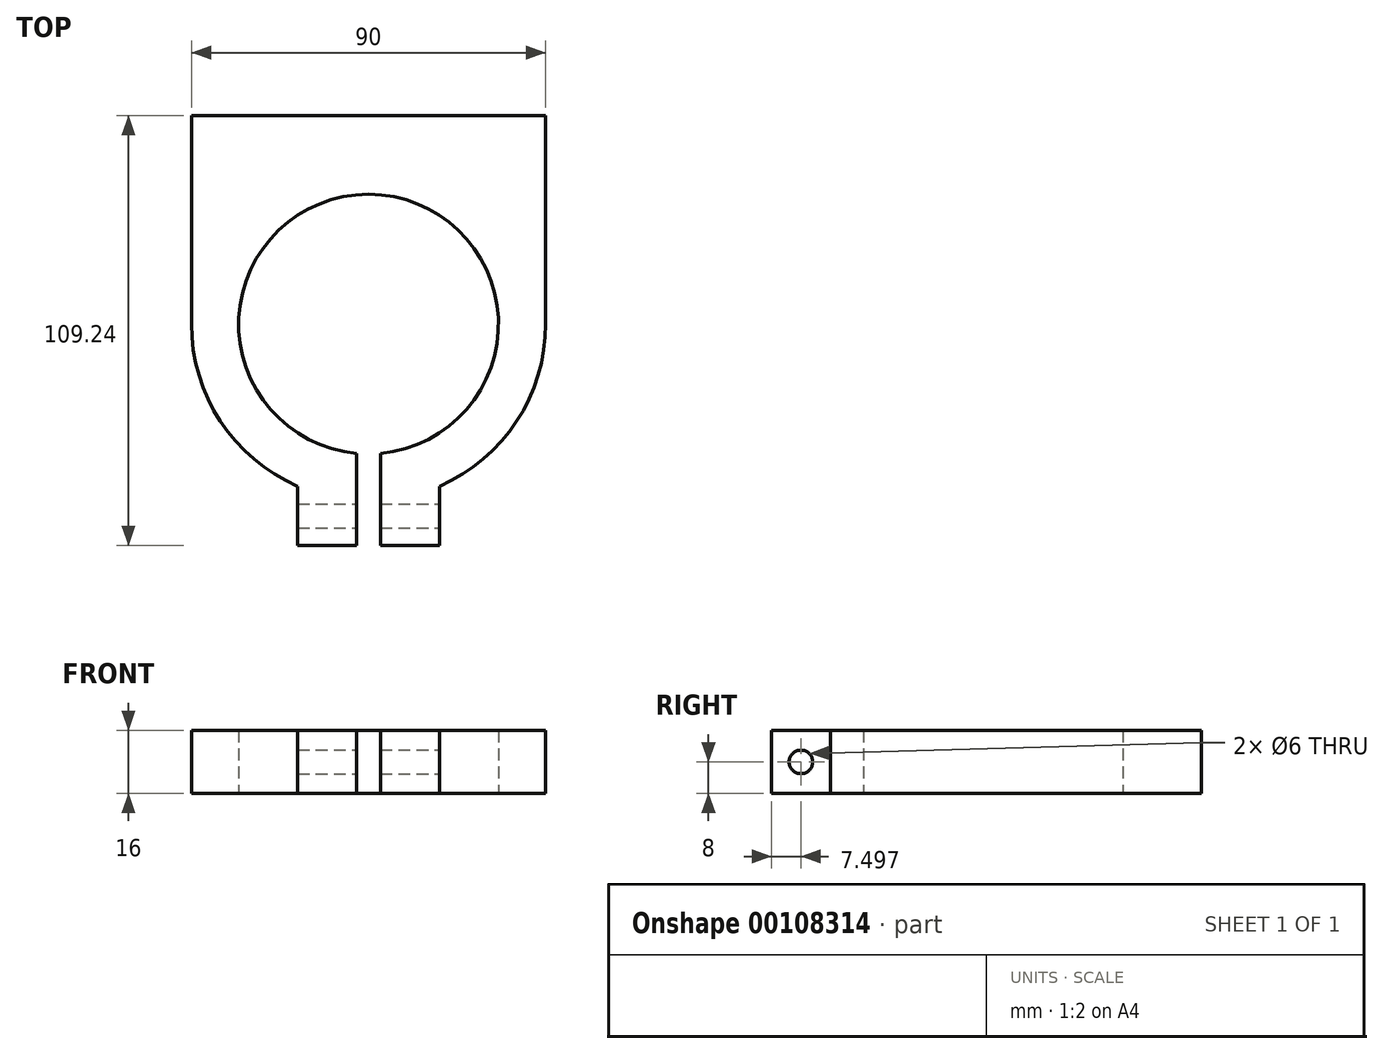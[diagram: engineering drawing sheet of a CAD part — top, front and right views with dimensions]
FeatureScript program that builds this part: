
annotation { "Feature Type Name" : "Feature", "Feature Type Description" : "" }
export const myFeature = defineFeature(function(context is Context, id is Id, definition is map)
    precondition{}
    {
        {
            var Q0;
            Q0=qCreatedBy(makeId("Top.planeOp"),FACE);
            var sketch = newSketch(context, id + "F0", { "sketchPlane" : qUnion([Q0])});
            skLineSegment(sketch, "E0", {"start": v(-45, 0) * mm, "end": v(-45, 53) * mm});
            skLineSegment(sketch, "E1", {"start": v(-45, 53) * mm, "end": v(0, 53) * mm});
            skLineSegment(sketch, "E2", {"start": v(-3, -32.86) * mm, "end": v(-3, -56.24) * mm});
            skLineSegment(sketch, "E3", {"start": v(-3, -56.24) * mm, "end": v(-18, -56.24) * mm});
            skLineSegment(sketch, "E4", {"start": v(-18, -56.24) * mm, "end": v(-18, -41.24) * mm});
            skArc(sketch, "E5", {"start": v(-3, -32.86) * mm, "mid": v(-32.97, 1.5) * mm, "end": v(0, 33) * mm});
            skArc(sketch, "E6", {"start": v(-45, 0) * mm, "mid": v(-37.65, -24.65) * mm, "end": v(-18, -41.24) * mm});
            skLineSegment(sketch, "E7.MirrorCS", {"start": v(18, -56.24) * mm, "end": v(18, -41.24) * mm});
            skArc(sketch, "E8.MirrorCS", {"start": v(3, -32.86) * mm, "mid": v(32.97, 1.5) * mm, "end": v(0, 33) * mm});
            skLineSegment(sketch, "E9.MirrorCS", {"start": v(45, 0) * mm, "end": v(45, 53) * mm});
            skArc(sketch, "E10.MirrorCS", {"start": v(45, 0) * mm, "mid": v(37.65, -24.65) * mm, "end": v(18, -41.24) * mm});
            skLineSegment(sketch, "E11.MirrorCS", {"start": v(45, 53) * mm, "end": v(0, 53) * mm});
            skLineSegment(sketch, "E12.MirrorCS", {"start": v(3, -32.86) * mm, "end": v(3, -56.24) * mm});
            skLineSegment(sketch, "E13.MirrorCS", {"start": v(3, -56.24) * mm, "end": v(18, -56.24) * mm});
            skSolve(sketch);
        }
        {
            var Q0;
            Q0=makeQuery(id+"F0.imprint","IMPRINT",FACE,{"disambiguationData":[TD([[makeQuery(id+"F0.imprint","IMPRINT",EDGE,{"derivedFrom":sQuery(id+"F0.wireOp",EDGE,"E0")}),-1.0]])]});
            extrude(context, id + "F1", {"entities" : qUnion([Q0]), "depth" : 16 * mm});
        }
        {
            var Q0;
            Q0=makeQuery(id+"F1.opExtrude","SWEPT_FACE",FACE,{"disambiguationData":[OSD([sQuery(id+"F0.wireOp",EDGE,"E7.MirrorCS")])]});
            var sketch = newSketch(context, id + "F2", { "sketchPlane" : qUnion([Q0])});
            skLineSegment(sketch, "E14", {"start": v(-56.24, 0) * mm, "end": v(-41.24, 16) * mm, "construction": true});
            skPoint(sketch, "E15", {"position": v(-48.74, 8) * mm});
            skSolve(sketch);
        }
        {
            var Q0;
            Q0=sQuery(id+"F2.wireOp",VERTEX,"E15");
            var Q1;
            Q1=makeQuery(id+"F1.opExtrude","SWEPT_BODY",BODY,{"disambiguationData":[OSD([sQuery(id+"F0.wireOp",EDGE,"E0"),sQuery(id+"F0.wireOp",EDGE,"E1"),sQuery(id+"F0.wireOp",EDGE,"E2"),sQuery(id+"F0.wireOp",EDGE,"E3"),sQuery(id+"F0.wireOp",EDGE,"E4"),sQuery(id+"F0.wireOp",EDGE,"E5"),sQuery(id+"F0.wireOp",EDGE,"E6"),sQuery(id+"F0.wireOp",EDGE,"E7.MirrorCS"),sQuery(id+"F0.wireOp",EDGE,"E8.MirrorCS"),sQuery(id+"F0.wireOp",EDGE,"E9.MirrorCS"),sQuery(id+"F0.wireOp",EDGE,"E10.MirrorCS"),sQuery(id+"F0.wireOp",EDGE,"E11.MirrorCS"),sQuery(id+"F0.wireOp",EDGE,"E12.MirrorCS"),sQuery(id+"F0.wireOp",EDGE,"E13.MirrorCS")])]});
            hole(context, id + "F3", {"style" : HoleStyle.SIMPLE, "endStyle" : HoleEndStyle.THROUGH, "holeDiameter" : 6 * mm, "locations" : qUnion([Q0]), "scope" : qUnion([Q1]), "isTappedThrough" : true});
        }
    });
